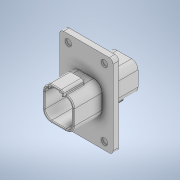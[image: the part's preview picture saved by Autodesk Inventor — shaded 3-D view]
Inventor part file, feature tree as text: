
AUTODESK INVENTOR PART (.ipt)
format: ipt  version: 2021 (Build 250183000, 183)  size: 521,216 bytes
history: native  units: in
note: dims shown in document units (in); Inventor stores cm internally (conversion verified against a paired STEP export)
features: sketch x1, imported_body x1
ambient origin geometry x8: Origin, YZ Plane, XZ Plane, XY Plane, X Axis, Y Axis, Z Axis, Center Point
bodies: Solid1 (feature_tree)
feature tree (2):
  sketch  "Sketch1"
  imported_body  "Base1"
